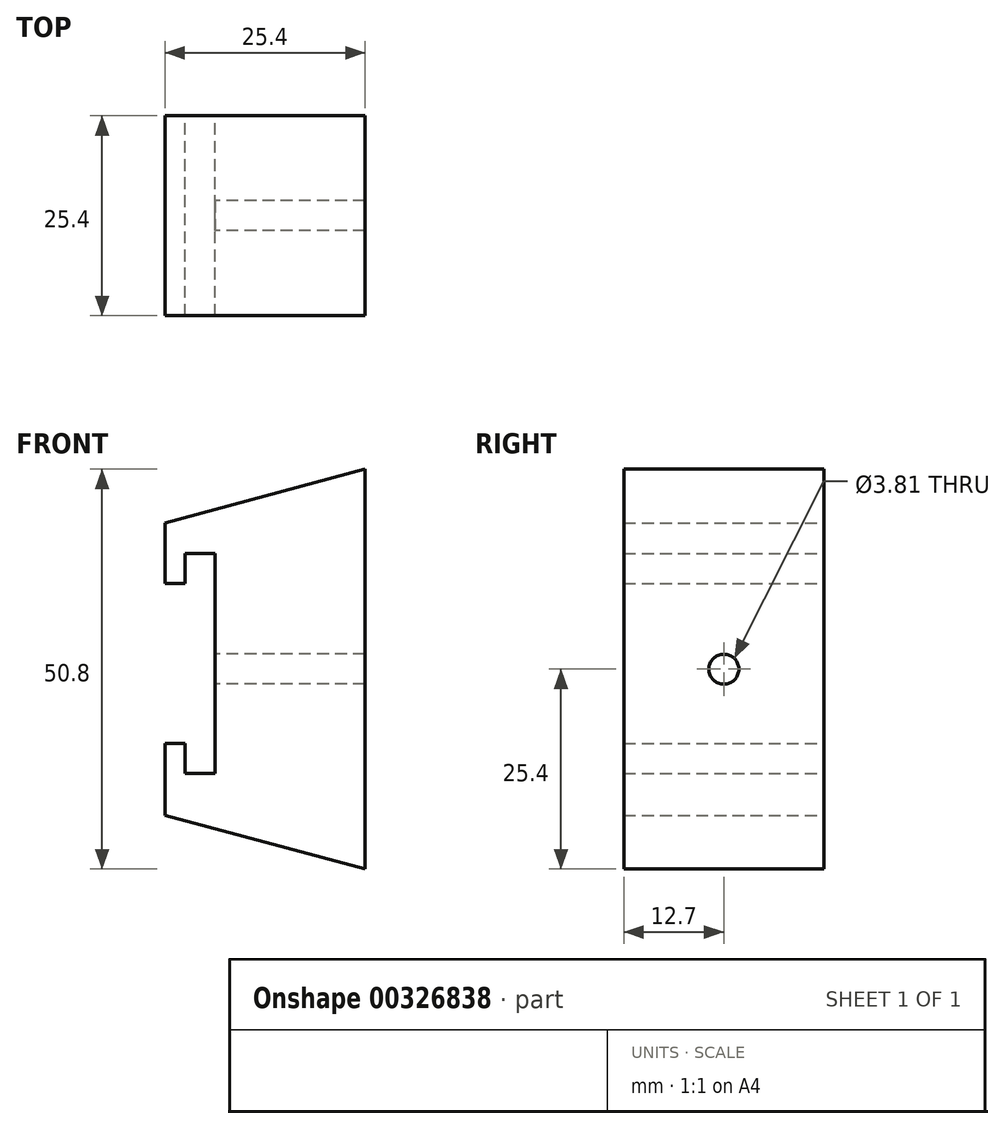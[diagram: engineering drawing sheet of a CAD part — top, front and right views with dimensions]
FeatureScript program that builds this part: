
annotation { "Feature Type Name" : "Feature", "Feature Type Description" : "" }
export const myFeature = defineFeature(function(context is Context, id is Id, definition is map)
    precondition{}
    {
        {
            var Q0;
            Q0=qCreatedBy(makeId("Front.planeOp"),FACE);
            var sketch = newSketch(context, id + "F0", { "sketchPlane" : qUnion([Q0])});
            skLineSegment(sketch, "E0", {"start": v(0, 0) * mm, "end": v(0, 27.94) * mm});
            skLineSegment(sketch, "E1", {"start": v(0, 27.94) * mm, "end": v(-3.81, 27.94) * mm});
            skLineSegment(sketch, "E2", {"start": v(-3.81, 27.94) * mm, "end": v(-3.81, 24.13) * mm});
            skLineSegment(sketch, "E3", {"start": v(-3.81, 24.13) * mm, "end": v(-6.35, 24.13) * mm});
            skLineSegment(sketch, "E4", {"start": v(-6.35, 24.13) * mm, "end": v(-6.35, 31.85) * mm});
            skLineSegment(sketch, "E5", {"start": v(-6.35, 31.85) * mm, "end": v(19.05, 38.66) * mm});
            skLineSegment(sketch, "E6", {"start": v(19.05, 38.66) * mm, "end": v(19.05, -12.14) * mm});
            skLineSegment(sketch, "E7", {"start": v(19.05, -12.14) * mm, "end": v(-6.35, -5.33) * mm});
            skLineSegment(sketch, "E8", {"start": v(-3.8, 3.8) * mm, "end": v(-3.8, 0) * mm});
            skLineSegment(sketch, "E9", {"start": v(-3.8, 0) * mm, "end": v(0, 0) * mm});
            skLineSegment(sketch, "E10", {"start": v(-3.8, 3.8) * mm, "end": v(-6.35, 3.8) * mm});
            skLineSegment(sketch, "E11", {"start": v(-6.35, 3.8) * mm, "end": v(-6.35, -5.33) * mm});
            skSolve(sketch);
        }
        {
            var Q0;
            Q0 = qSketchRegion(id + "F0", true);
            extrude(context, id + "F1", {"entities" : qUnion([Q0]), "endBound" : BoundingType.SYMMETRIC, "depth" : 25.4 * mm});
        }
        {
            var Q0;
            Q0=makeQuery(id+"F1.opExtrude","SWEPT_FACE",FACE,{"disambiguationData":[OSD([sQuery(id+"F0.wireOp",EDGE,"E0")])]});
            var sketch = newSketch(context, id + "F2", { "sketchPlane" : qUnion([Q0])});
            skPoint(sketch, "E12", {"position": v(0, 13.26) * mm});
            skSolve(sketch);
        }
        {
            var Q0;
            Q0=sQuery(id+"F2.wireOp",VERTEX,"E12");
            var Q1;
            Q1=makeQuery(id+"F1.opExtrude","SWEPT_BODY",BODY,{"disambiguationData":[OSD([sQuery(id+"F0.wireOp",EDGE,"E0"),sQuery(id+"F0.wireOp",EDGE,"E1"),sQuery(id+"F0.wireOp",EDGE,"E2"),sQuery(id+"F0.wireOp",EDGE,"E3"),sQuery(id+"F0.wireOp",EDGE,"E4"),sQuery(id+"F0.wireOp",EDGE,"E5"),sQuery(id+"F0.wireOp",EDGE,"E6"),sQuery(id+"F0.wireOp",EDGE,"E7"),sQuery(id+"F0.wireOp",EDGE,"E8"),sQuery(id+"F0.wireOp",EDGE,"E9"),sQuery(id+"F0.wireOp",EDGE,"E10"),sQuery(id+"F0.wireOp",EDGE,"E11")])]});
            hole(context, id + "F3", {"style" : HoleStyle.SIMPLE, "endStyle" : HoleEndStyle.THROUGH, "holeDiameter" : 3.8 * mm, "tappedDepth" : 12.7 * mm, "tapClearance" : 3, "locations" : qUnion([Q0]), "scope" : qUnion([Q1])});
        }
    });
